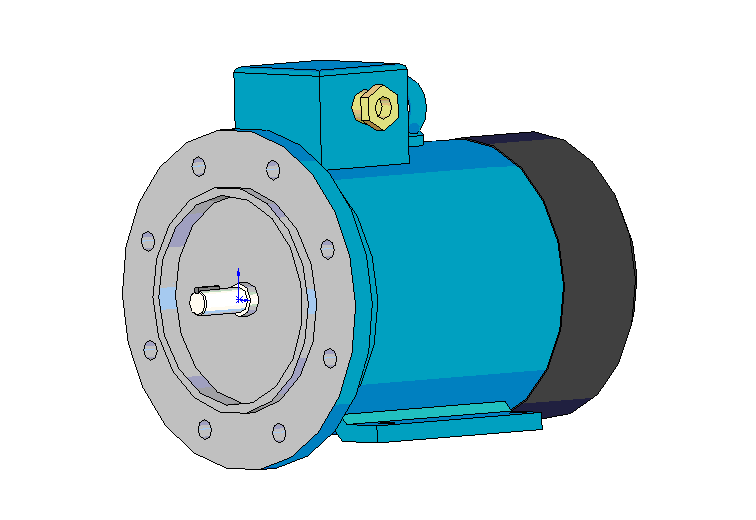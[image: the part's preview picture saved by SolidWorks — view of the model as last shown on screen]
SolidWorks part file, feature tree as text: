
SOLIDWORKS PART (.sldprt)
format: sldprt  version: not decoded by parser v0  size: 865,280 bytes
history: native  units: mm
features: sketch x19, extrude x13, plane x5, chamfer x4, cut_extrude x4, material x1, fillet x1, sweep x1 (+10 scaffold rows collapsed)
feature tree (58):
  scaffold x10  (default folders/planes/origin — collapsed)
  material  "Ст.3 ГОСТ 380-88"
  plane  "Спереди"
  plane  "Сверху"
  plane  "Справа"
  sketch  "Эскиз1"  dims[D1=9.0mm]
  extrude  "Вытянуть1"  Depth=20mm
  chamfer  "Фаска1"  Distance=0.5mm Angle=45deg
  sketch  "Эскиз2"  dims[D1=2.0mm D2=2.0mm D3=5.5mm]
  extrude  "Вытянуть2"  Depth=10mm
  sketch  "Эскиз3"  dims[D1=12.0mm]
  extrude  "Вытянуть3"  Depth=4mm
  chamfer  "Фаска2"  Distance=0.5mm Angle=45deg
  sketch  "Эскиз4"  dims[c1.D1=~9.646492mm c1.D2=80.0mm c2.D1=3.0mm]
  extrude  "Вытянуть4"  Depth=8mm
  sketch  "Эскиз5"  dims[D1=120.0mm]
  extrude  "Вытянуть5"  Depth=4mm
  sketch  "Эскиз6"  dims[c1.D2=7.0mm c1.D4=7.0mm c1.D1=~66.356099mm c2.D1=22.5deg c2.D3=50.0mm c2.D5=50.0mm c2.D6=50.0mm]
  cut_extrude  "Вырез-Вытянуть1"  [1 undecoded]
  sketch  "Эскиз7"  dims[D1=84.0mm]
  extrude  "Вытянуть6"  Depth=12mm
  sketch  "Эскиз8"  dims[D2=60.0mm D1=0.0mm]
  extrude  "Вытянуть7"  Depth=89mm
  sketch  "Эскиз9"  dims[D1=101.0mm]
  extrude  "Вытянуть8"  Depth=45mm
  chamfer  "Фаска3"  Distance=11mm Angle=45deg
  sketch  "Эскиз11"  dims[c1.D1=50.0mm c1.D2=6.0mm c1.D3=96.0mm c1.D4=40.0mm c1.D5=40.0mm c1.D6=30.0mm c1.D7=30.0mm c1.D8=6.0mm c1.D9=6.0mm c1.D10=~8.664811mm c2.D10=45.0deg c2.D11=~69.010922mm c3.D11=45.0deg]
  extrude  "Вытянуть9"  Depth=79mm
  sketch  "Эскиз12"  dims[c1.D1=5.8mm c1.D5=5.8mm c1.D6=5.8mm c1.D7=5.8mm c1.D2=52.0mm c1.D3=40.0mm c1.D4=90.0deg c2.D5=63.0mm c2.D6=80.0mm c2.D7=63.0mm]
  cut_extrude  "Вырез-Вытянуть2"  [1 undecoded]
  sketch  "Эскиз13"  dims[c1.D1=38.0mm c1.D2=44.0mm c2.D1=0.5mm c2.D3=42.0mm]
  extrude  "Вытянуть10"  Depth=80mm
  fillet  "Скругление1"  Radius=2mm
  sketch  "Эскиз14"  dims[D1=12.0mm D2=14.0mm D3=21.0mm]
  extrude  "Вытянуть11"  Depth=6mm
  sketch  "Эскиз15"  dims[D1=14.0mm D2=7.0mm]
  extrude  "Вытянуть12"  Depth=4mm
  sketch  "Эскиз16"  dims[D1=8.0mm]
  cut_extrude  "Вырез-Вытянуть3"  Depth=5mm
  plane  "Плоскость1"  Offset=50mm
  sketch  "Эскиз17"  dims[D1=15.0mm D2=80.0mm]
  extrude  "Вытянуть13"  Depth=5mm
  chamfer  "Фаска4"  Distance=2mm Angle=45deg
  plane  "Плоскость3"  Offset=80mm
  sketch  "Эскиз19"  dims[D1=17.0mm D2=63.0mm]
  sketch  "Эскиз21"  dims[D1=6.0mm D2=~8.403693mm]
  sweep  "По траектории1"
  sketch  "Эскиз22"  dims[D1=74.0mm D2=12.0mm]
  cut_extrude  "Вырез-Вытянуть4"  Depth=4mm
decode coverage: 39 of 42 modeling features carry decoded parameters
note: ~ marks probable driven/reference dimensions
note: 2 parameter values undecoded
note: suppression state not decoded; provenance and decode notes live in map.json
